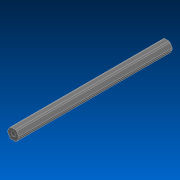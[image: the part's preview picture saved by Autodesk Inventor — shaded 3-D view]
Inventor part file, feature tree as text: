
AUTODESK INVENTOR PART (.ipt)
format: ipt  version: 2022.2 (Build 262287000, 287)  size: 122,368 bytes
history: native  units: in
note: dims shown in document units (in); Inventor stores cm internally (conversion verified against a paired STEP export)
features: extrude x1, sketch x1, other x1
ambient origin geometry x8: Origin, YZ Plane, XZ Plane, XY Plane, X Axis, Y Axis, Z Axis, Center Point
bodies: Solid1 (feature_tree)
feature tree (3):
  extrude  "Extrusion1"  TaperAngle=0.0deg  [1 undecoded]
  sketch  "Sketch1"  dims[d0=28.5in d1=0.0in]
  other  "Cut-Extrude2"
note: 1 required parameter value undecoded (feature->parameter linkage not recoverable at this tier; creation-order binding heuristic only, values carry confidence <= 0.55)
